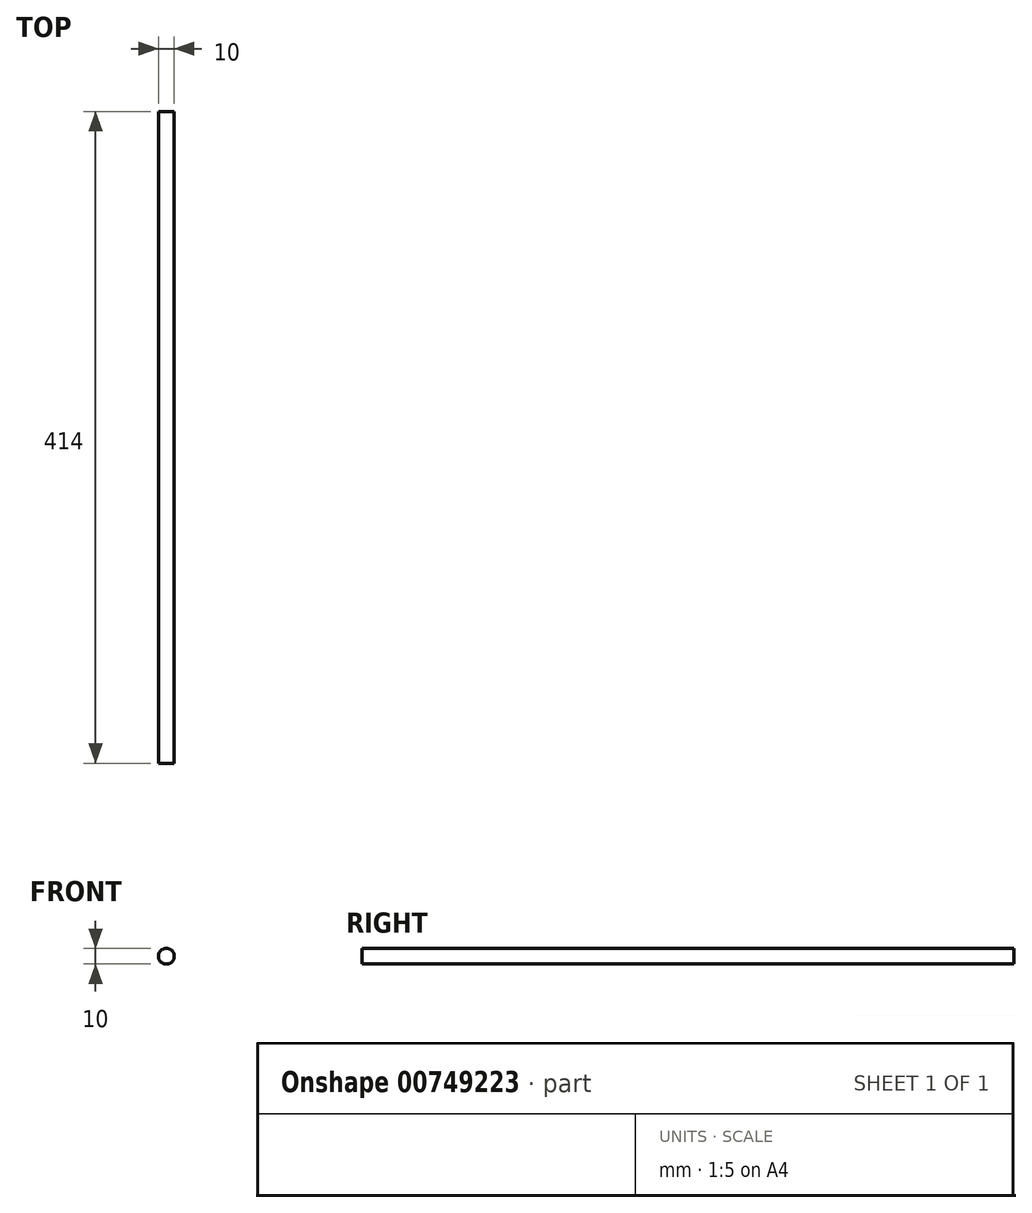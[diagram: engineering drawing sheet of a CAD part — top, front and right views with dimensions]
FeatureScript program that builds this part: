
annotation { "Feature Type Name" : "Feature", "Feature Type Description" : "" }
export const myFeature = defineFeature(function(context is Context, id is Id, definition is map)
    precondition{}
    {
        {
            var Q0;
            Q0=qCreatedBy(makeId("Front.planeOp"),FACE);
            var sketch = newSketch(context, id + "F0", { "sketchPlane" : qUnion([Q0])});
            skCircle(sketch, "E0", {"center": v(0, 0) * mm, "radius": 5 * mm});
            skSolve(sketch);
        }
        {
            var Q0;
            Q0=qSketchRegion(id+"F0",true);
            extrude(context, id + "F1", {"entities" : qUnion([Q0]), "depth" : 414 * mm, "offsetDistance" : 25.4 * mm});
        }
    });
